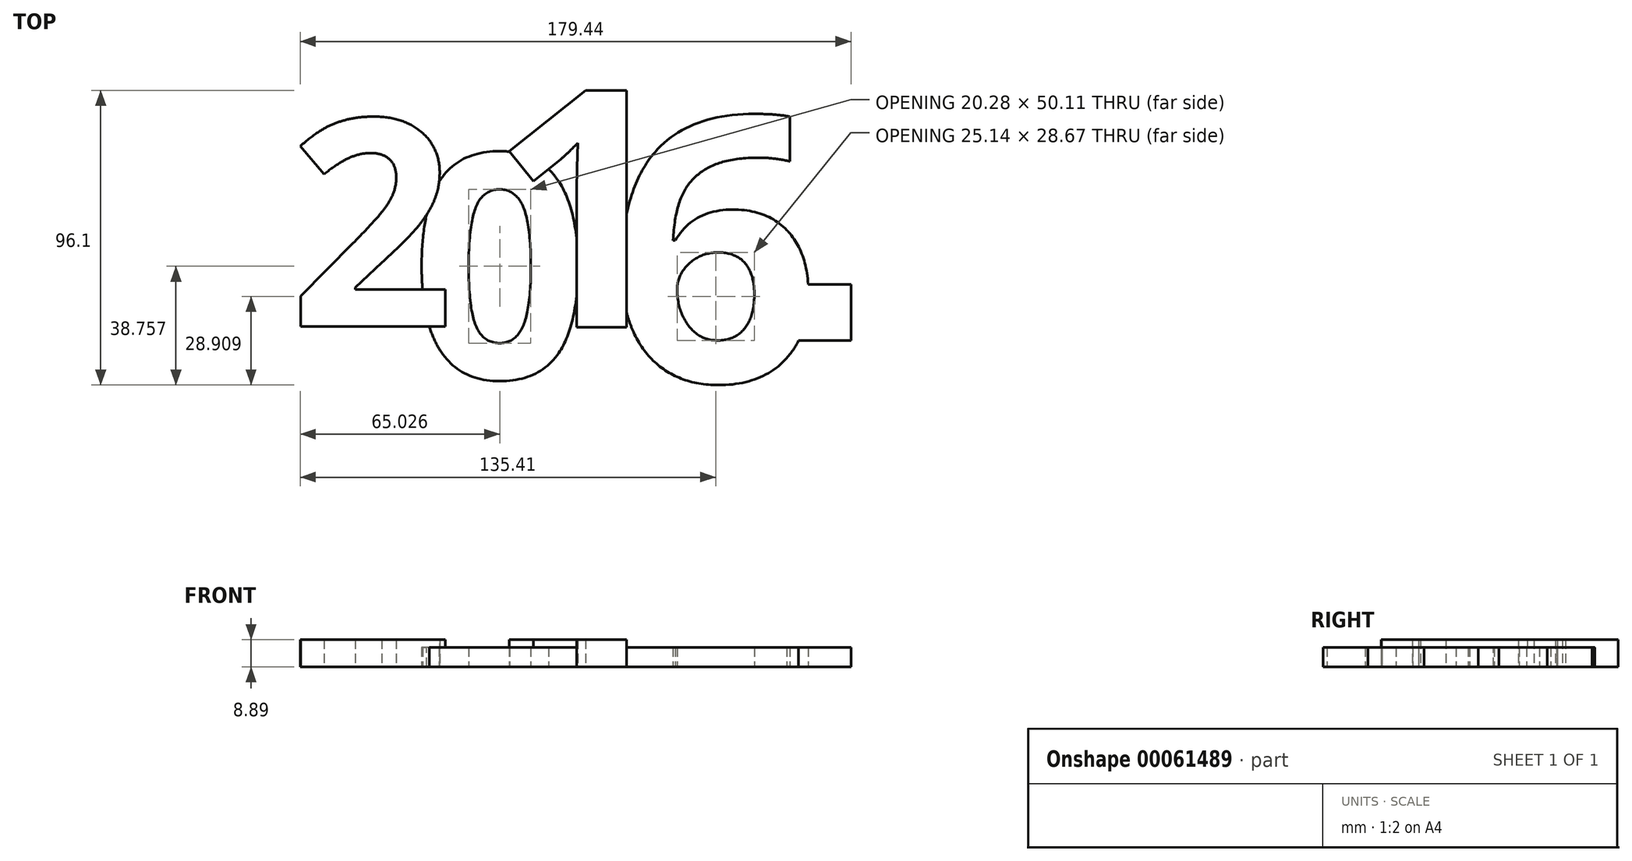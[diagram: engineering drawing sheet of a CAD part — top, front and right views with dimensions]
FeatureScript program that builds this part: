
annotation { "Feature Type Name" : "Feature", "Feature Type Description" : "" }
export const myFeature = defineFeature(function(context is Context, id is Id, definition is map)
    precondition{}
    {
        {
            var Q0;
            Q0=qCreatedBy(makeId("Top.planeOp"),FACE);
            var sketch = newSketch(context, id + "F0", { "sketchPlane" : qUnion([Q0])});
            skPoint(sketch, "E0.rect.middle", {"position": v(0, 0) * mm});
            skText(sketch, "E1", { "text": "2", "fontName": "NotoSans-Bold.ttf"});
            skText(sketch, "E2", { "text": "0", "fontName": "NotoSans-Bold.ttf"});
            skText(sketch, "E3", { "text": "1", "fontName": "NotoSans-Bold.ttf"});
            skText(sketch, "E4", { "text": "6", "fontName": "NotoSans-Bold.ttf"});
            skText(sketch, "E5", { "text": "!", "fontName": "RobotoSlab-Bold.ttf"});
            const initialGuessF0  = {"E1": [-0.08606, -0.01685, 1, 0, 0.06806], "E2": [-0.04656, -0.03368, 1, 0, 0.07346], "E3": [-0.02077, -0.0171, 1, 0, 0.07789], "E4": [0.01803, -0.03478, 1, 0, 0.08698], "E5": [0.0676, -0.0214, 1, 0, 0.10543]};
            skSetInitialGuess(sketch, initialGuessF0);
            skSolve(sketch);
        }
        {
            var Q0;
            {var subQ11=sQuery(id+"F0.wireOp",EDGE,"E1.sketch_text.stroke-1");Q0=makeQuery(id+"F0.imprint","IMPRINT",FACE,{"disambiguationData":[TD([[makeQuery(id+"F0.imprint","IMPRINT",EDGE,{"derivedFrom":subQ11}),-1.0]])]});}
            var Q1;
            {var subQ0=sQuery(id+"F0.wireOp",EDGE,"E1.sketch_text.stroke-23");Q1=makeQuery(id+"F0.imprint","IMPRINT",FACE,{"disambiguationData":[TD([[makeQuery(id+"F0.imprint","IMPRINT",EDGE,{"derivedFrom":subQ0}),-1.0]])]});}
            var Q2;
            {var subQ6=sQuery(id+"F0.wireOp",EDGE,"E1.sketch_text.stroke-23");Q2=makeQuery(id+"F0.imprint","IMPRINT",FACE,{"disambiguationData":[TD([[makeQuery(id+"F0.imprint","IMPRINT",EDGE,{"derivedFrom":subQ6}),1.0]])]});}
            var Q3;
            {var subQ6=sQuery(id+"F0.wireOp",EDGE,"E3.sketch_text.stroke-0");Q3=makeQuery(id+"F0.imprint","IMPRINT",FACE,{"disambiguationData":[TD([[makeQuery(id+"F0.imprint","IMPRINT",EDGE,{"derivedFrom":subQ6}),-1.0]])]});}
            var Q4;
            {var subQ3=sQuery(id+"F0.wireOp",EDGE,"E4.sketch_text.stroke-1");Q4=makeQuery(id+"F0.imprint","IMPRINT",FACE,{"disambiguationData":[TD([[makeQuery(id+"F0.imprint","IMPRINT",EDGE,{"derivedFrom":subQ3}),-1.0]])]});}
            var Q5;
            {var subQ1=sQuery(id+"F0.wireOp",EDGE,"E3.sketch_text.stroke-9");var subQ3=sQuery(id+"F0.wireOp",EDGE,"E4.sketch_text.stroke-0");var subQ5=makeQuery(id+"F0.imprint","INTERSECT",VERTEX,{"derivedFrom":[subQ1,subQ3]});Q5=makeQuery(id+"F0.imprint","IMPRINT",FACE,{"disambiguationData":[TD([[makeQuery(id+"F0.imprint","IMPRINT",EDGE,{"disambiguationData":[TD([[subQ5,-1.0]])],"derivedFrom":subQ1}),-1.0]])]});}
            var Q6;
            {var subQ1=sQuery(id+"F0.wireOp",EDGE,"E2.sketch_text.stroke-7");var subQ3=sQuery(id+"F0.wireOp",EDGE,"E2.sketch_text.stroke-0");var subQ5=makeQuery(id+"F0.imprint","INTERSECT",VERTEX,{"derivedFrom":[subQ3,subQ1]});Q6=makeQuery(id+"F0.imprint","IMPRINT",FACE,{"disambiguationData":[TD([[makeQuery(id+"F0.imprint","IMPRINT",EDGE,{"disambiguationData":[TD([[subQ5,-1.0]])],"derivedFrom":subQ3}),-1.0]])]});}
            var Q7;
            {var subQ0=sQuery(id+"F0.wireOp",EDGE,"E3.sketch_text.stroke-6");var subQ1=sQuery(id+"F0.wireOp",EDGE,"E2.sketch_text.stroke-6");var subQ2=makeQuery(id+"F0.imprint","INTERSECT",VERTEX,{"derivedFrom":[subQ1,subQ0]});Q7=makeQuery(id+"F0.imprint","IMPRINT",FACE,{"disambiguationData":[TD([[makeQuery(id+"F0.imprint","IMPRINT",EDGE,{"disambiguationData":[TD([[subQ2,-1.0]])],"derivedFrom":subQ1}),-1.0]])]});}
            var Q8;
            {var subQ1=sQuery(id+"F0.wireOp",EDGE,"E1.sketch_text.stroke-18");var subQ3=sQuery(id+"F0.wireOp",EDGE,"E1.sketch_text.stroke-17");var subQ5=makeQuery(id+"F0.imprint","INTERSECT",VERTEX,{"derivedFrom":[subQ3,subQ1]});Q8=makeQuery(id+"F0.imprint","IMPRINT",FACE,{"disambiguationData":[TD([[makeQuery(id+"F0.imprint","IMPRINT",EDGE,{"disambiguationData":[TD([[subQ5,1.0]])],"derivedFrom":subQ3}),-1.0]])]});}
            var Q9;
            {var subQ0=sQuery(id+"F0.wireOp",EDGE,"E5.sketch_text.stroke-7");Q9=makeQuery(id+"F0.imprint","IMPRINT",FACE,{"disambiguationData":[TD([[makeQuery(id+"F0.imprint","IMPRINT",EDGE,{"derivedFrom":subQ0}),-1.0]])]});}
            var Q10;
            {var subQ3=sQuery(id+"F0.wireOp",EDGE,"E5.sketch_text.stroke-5");Q10=makeQuery(id+"F0.imprint","IMPRINT",FACE,{"disambiguationData":[TD([[makeQuery(id+"F0.imprint","IMPRINT",EDGE,{"derivedFrom":subQ3}),-1.0]])]});}
            var Q11;
            {var subQ5=sQuery(id+"F0.wireOp",EDGE,"E4.sketch_text.stroke-3");Q11=makeQuery(id+"F0.imprint","IMPRINT",FACE,{"disambiguationData":[TD([[makeQuery(id+"F0.imprint","IMPRINT",EDGE,{"derivedFrom":subQ5}),-1.0]])]});}
            extrude(context, id + "F1", {"entities" : qUnion([Q0, Q1, Q2, Q3, Q4, Q5, Q6, Q7, Q8, Q9, Q10, Q11]), "depth" : 6.35 * mm});
        }
        {
            var Q0;
            {var subQ11=sQuery(id+"F0.wireOp",EDGE,"E1.sketch_text.stroke-1");Q0=makeQuery(id+"F0.imprint","IMPRINT",FACE,{"disambiguationData":[TD([[makeQuery(id+"F0.imprint","IMPRINT",EDGE,{"derivedFrom":subQ11}),-1.0]])]});}
            var Q1;
            {var subQ1=sQuery(id+"F0.wireOp",EDGE,"E1.sketch_text.stroke-18");var subQ3=sQuery(id+"F0.wireOp",EDGE,"E1.sketch_text.stroke-17");var subQ5=makeQuery(id+"F0.imprint","INTERSECT",VERTEX,{"derivedFrom":[subQ3,subQ1]});Q1=makeQuery(id+"F0.imprint","IMPRINT",FACE,{"disambiguationData":[TD([[makeQuery(id+"F0.imprint","IMPRINT",EDGE,{"disambiguationData":[TD([[subQ5,1.0]])],"derivedFrom":subQ3}),-1.0]])]});}
            var Q2;
            {var subQ0=sQuery(id+"F0.wireOp",EDGE,"E1.sketch_text.stroke-23");Q2=makeQuery(id+"F0.imprint","IMPRINT",FACE,{"disambiguationData":[TD([[makeQuery(id+"F0.imprint","IMPRINT",EDGE,{"derivedFrom":subQ0}),-1.0]])]});}
            extrude(context, id + "F2", {"entities" : qUnion([Q0, Q1, Q2]), "operationType" : NewBodyOperationType.ADD, "depth" : 8.9 * mm});
        }
        {
            var Q0;
            {var subQ0=sQuery(id+"F0.wireOp",EDGE,"E3.sketch_text.stroke-6");var subQ1=sQuery(id+"F0.wireOp",EDGE,"E2.sketch_text.stroke-6");var subQ2=makeQuery(id+"F0.imprint","INTERSECT",VERTEX,{"derivedFrom":[subQ1,subQ0]});Q0=makeQuery(id+"F0.imprint","IMPRINT",FACE,{"disambiguationData":[TD([[makeQuery(id+"F0.imprint","IMPRINT",EDGE,{"disambiguationData":[TD([[subQ2,-1.0]])],"derivedFrom":subQ1}),-1.0]])]});}
            var Q1;
            {var subQ6=sQuery(id+"F0.wireOp",EDGE,"E3.sketch_text.stroke-0");Q1=makeQuery(id+"F0.imprint","IMPRINT",FACE,{"disambiguationData":[TD([[makeQuery(id+"F0.imprint","IMPRINT",EDGE,{"derivedFrom":subQ6}),-1.0]])]});}
            var Q2;
            {var subQ1=sQuery(id+"F0.wireOp",EDGE,"E3.sketch_text.stroke-9");var subQ3=sQuery(id+"F0.wireOp",EDGE,"E4.sketch_text.stroke-0");var subQ5=makeQuery(id+"F0.imprint","INTERSECT",VERTEX,{"derivedFrom":[subQ1,subQ3]});Q2=makeQuery(id+"F0.imprint","IMPRINT",FACE,{"disambiguationData":[TD([[makeQuery(id+"F0.imprint","IMPRINT",EDGE,{"disambiguationData":[TD([[subQ5,-1.0]])],"derivedFrom":subQ1}),-1.0]])]});}
            var Q3;
            {var subQ1=sQuery(id+"F0.wireOp",EDGE,"E2.sketch_text.stroke-7");var subQ3=sQuery(id+"F0.wireOp",EDGE,"E2.sketch_text.stroke-0");var subQ5=makeQuery(id+"F0.imprint","INTERSECT",VERTEX,{"derivedFrom":[subQ3,subQ1]});Q3=makeQuery(id+"F0.imprint","IMPRINT",FACE,{"disambiguationData":[TD([[makeQuery(id+"F0.imprint","IMPRINT",EDGE,{"disambiguationData":[TD([[subQ5,-1.0]])],"derivedFrom":subQ3}),-1.0]])]});}
            extrude(context, id + "F3", {"entities" : qUnion([Q0, Q1, Q2, Q3]), "operationType" : NewBodyOperationType.ADD, "depth" : 8.9 * mm});
        }
    });
